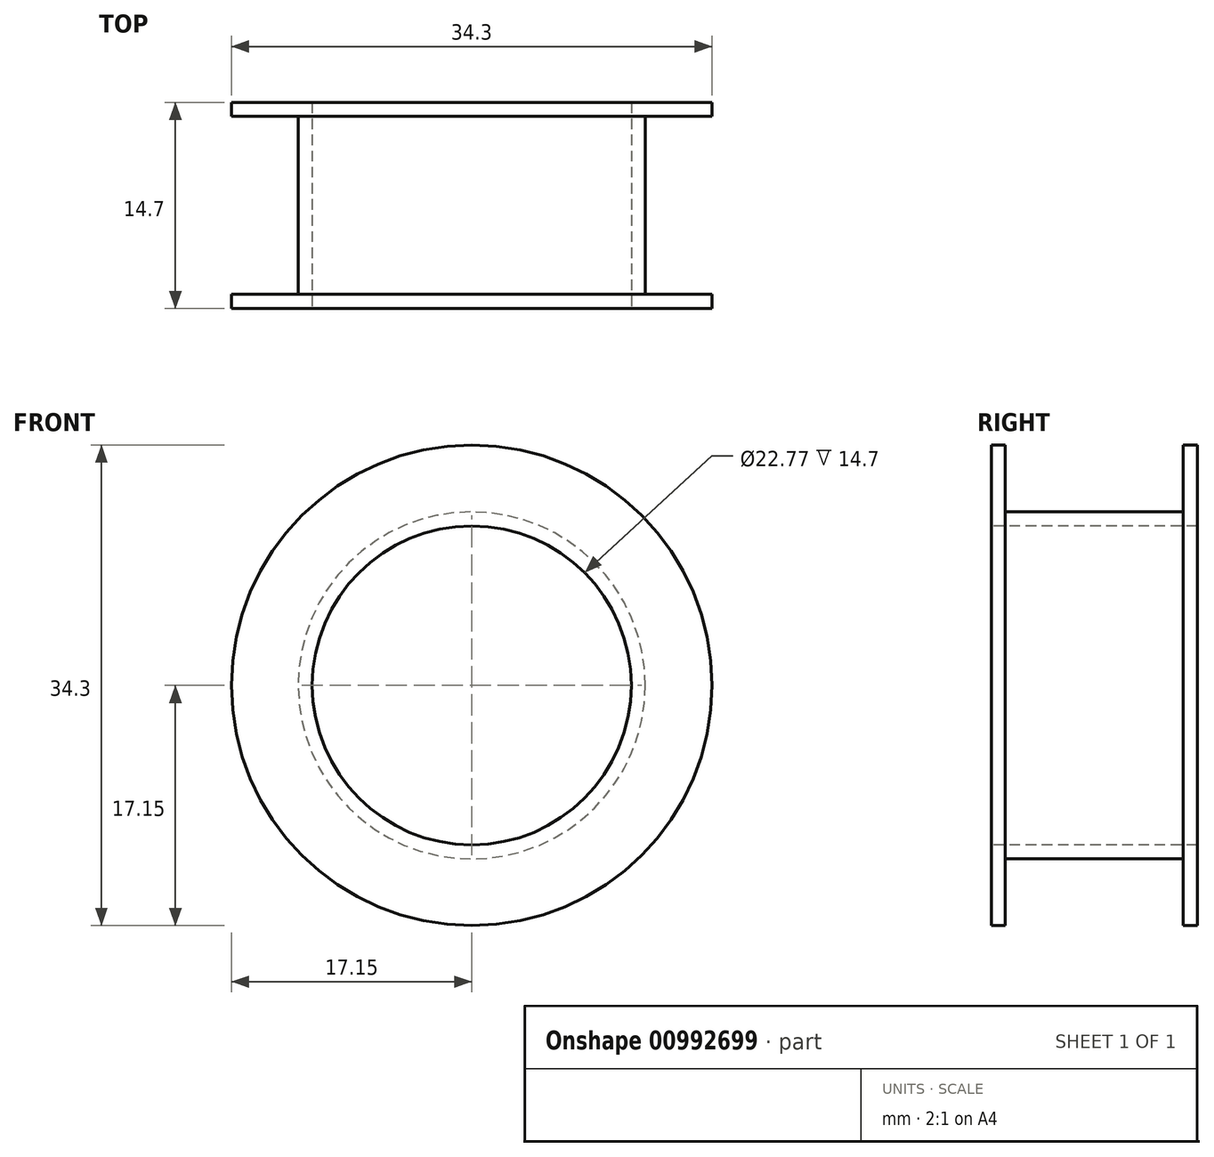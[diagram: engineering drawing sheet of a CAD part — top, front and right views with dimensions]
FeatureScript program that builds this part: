
annotation { "Feature Type Name" : "Feature", "Feature Type Description" : "" }
export const myFeature = defineFeature(function(context is Context, id is Id, definition is map)
    precondition{}
    {
        {
            var Q0;
            Q0=qCreatedBy(makeId("Top.planeOp"),FACE);
            var sketch = newSketch(context, id + "F0", { "sketchPlane" : qUnion([Q0])});
            skLineSegment(sketch, "E0", {"start": v(0, 0) * mm, "end": v(17.14, 0) * mm, "construction": true});
            skCircle(sketch, "E1", {"center": v(0, 0) * mm, "radius": 8.9 * mm, "construction": true});
            skLineSegment(sketch, "E2", {"start": v(17.15, 6.35) * mm, "end": v(12.38, 6.35) * mm});
            skLineSegment(sketch, "E3", {"start": v(17.15, -6.35) * mm, "end": v(12.38, -6.35) * mm});
            skLineSegment(sketch, "E4", {"start": v(0, -15.82) * mm, "end": v(0, 21.52) * mm, "construction": true});
            skLineSegment(sketch, "E5.0", {"start": v(17.15, -7.35) * mm, "end": v(11.38, -7.35) * mm});
            skLineSegment(sketch, "E5.2", {"start": v(17.15, 7.35) * mm, "end": v(11.38, 7.35) * mm});
            skLineSegment(sketch, "E6", {"start": v(17.15, 7.35) * mm, "end": v(17.15, 6.35) * mm});
            skLineSegment(sketch, "E7", {"start": v(17.14, -6.35) * mm, "end": v(17.15, -7.35) * mm});
            skLineSegment(sketch, "E8", {"start": v(11.38, 7.35) * mm, "end": v(11.38, -7.35) * mm});
            skLineSegment(sketch, "E9", {"start": v(12.38, 6.35) * mm, "end": v(12.38, -6.35) * mm});
            skSolve(sketch);
        }
        {
            var Q0;
            Q0=qSketchRegion(id+"F0",true);
            var Q1;
            Q1=sQuery(id+"F0.wireOp",EDGE,"E4");
            revolve(context, id + "F1", {"entities" : qUnion([Q0]), "axis" : qUnion([Q1]), "revolveType" : RevolveType.FULL});
        }
    });
